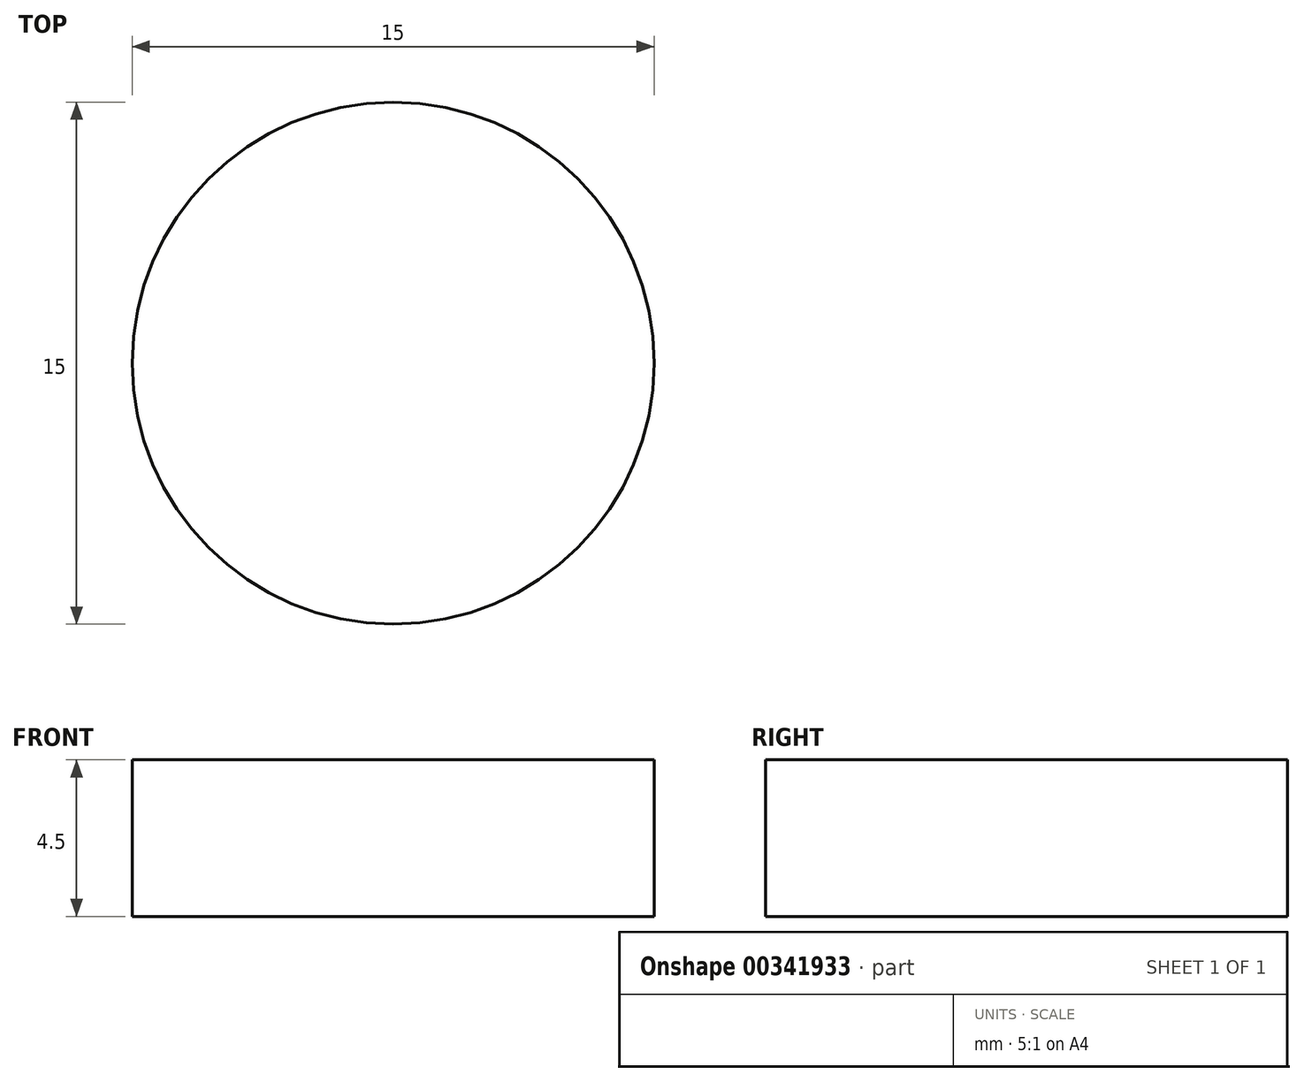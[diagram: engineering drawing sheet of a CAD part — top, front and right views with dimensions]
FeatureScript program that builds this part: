
annotation { "Feature Type Name" : "Feature", "Feature Type Description" : "" }
export const myFeature = defineFeature(function(context is Context, id is Id, definition is map)
    precondition{}
    {
        {
            var Q0;
            Q0=qCreatedBy(makeId("Top.planeOp"),FACE);
            var sketch = newSketch(context, id + "F0", { "sketchPlane" : qUnion([Q0])});
            skCircle(sketch, "E0", {"center": v(0, 0) * mm, "radius": 7.5 * mm});
            skSolve(sketch);
        }
        {
            var Q0;
            Q0 = qSketchRegion(id + "F0", true);
            extrude(context, id + "F1", {"entities" : qUnion([Q0]), "depth" : 4.5 * mm});
        }
    });
